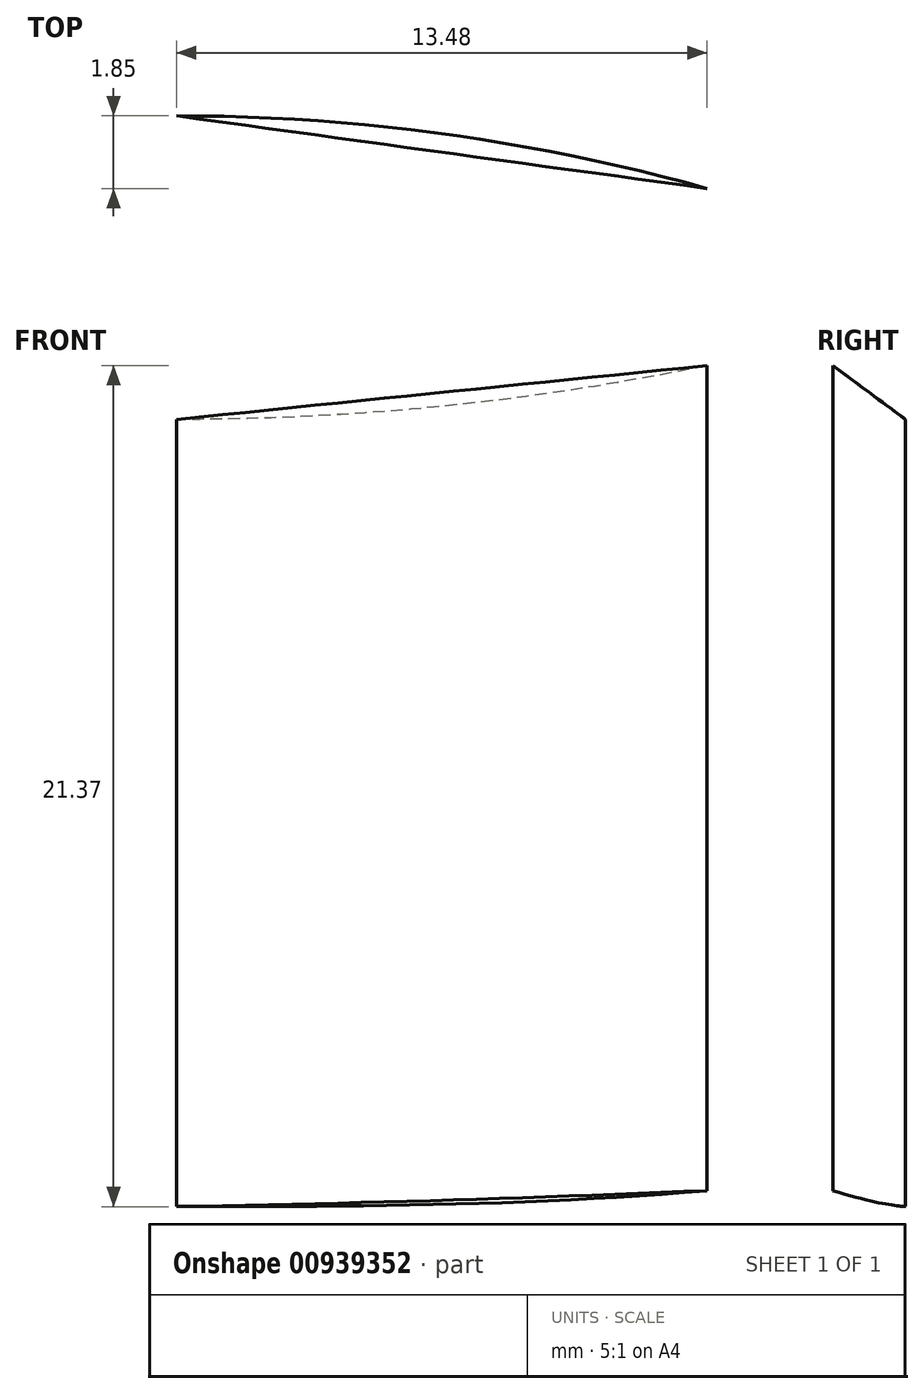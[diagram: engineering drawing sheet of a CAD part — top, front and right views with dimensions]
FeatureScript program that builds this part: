
annotation { "Feature Type Name" : "Feature", "Feature Type Description" : "" }
export const myFeature = defineFeature(function(context is Context, id is Id, definition is map)
    precondition{}
    {
        {
            var Q0;
            Q0=qCreatedBy(makeId("Top.planeOp"),FACE);
            var sketch = newSketch(context, id + "F0", { "sketchPlane" : qUnion([Q0])});
            skCircle(sketch, "E0", {"center": v(0, 0) * mm, "radius": 100 * mm, "construction": true});
            skLineSegment(sketch, "E1", {"start": v(0, 0) * mm, "end": v(4000, 0) * mm, "construction": true});
            skLineSegment(sketch, "E2", {"start": v(4000, 82.45) * mm, "end": v(4000, -88.42) * mm});
            skPoint(sketch, "E3.startSnap0", {"position": v(2000, 0) * mm});
            skEllipticalArc(sketch, "E4", {});
            skEllipticalArc(sketch, "E5", {});
            skLineSegment(sketch, "E6", {"start": v(500, 231.33) * mm, "end": v(500, -148.82) * mm, "construction": true});
            skLineSegment(sketch, "E7", {"start": v(2000, 216.5) * mm, "end": v(2000, -129.9) * mm, "construction": true});
            skLineSegment(sketch, "E8", {"start": v(3700, 95) * mm, "end": v(3700, -57) * mm, "construction": true});
            skFitSpline(sketch, "E9", {"points": [v(0, 100) * mm, v(166.45, 98.38) * mm, v(342.45, 195.8) * mm, v(973.63, 242.48) * mm], "startDerivative": vector(710.27, -109.76) * mm, "endDerivative": vector(1535.3, -24.16) * mm});
            skLineSegment(sketch, "E10", {"start": v(0, 100) * mm, "end": v(0, -150) * mm});
            const initialGuessF0  = {"E4": [0, 0, 1, 0, 4, 0.25, 0, 1.3393864335799355], "E5": [0, 0, 1, 0, 4, 0.15, 4.71238898038469, 0]};
            skSetInitialGuess(sketch, initialGuessF0);
            skSolve(sketch);
        }
        {
            var Q0;
            Q0=qCreatedBy(makeId("Right.planeOp"),FACE);
            cPlane(context, id + "F1", {"entities" : qUnion([Q0]), "cplaneType" : CPlaneType.OFFSET, "offset" : 500 * mm, "width" : 150 * mm, "height" : 150 * mm});
        }
        {
            var Q0;
            Q0=qCreatedBy(makeId("Right.planeOp"),FACE);
            cPlane(context, id + "F2", {"entities" : qUnion([Q0]), "cplaneType" : CPlaneType.OFFSET, "offset" : 2000 * mm, "width" : 150 * mm, "height" : 150 * mm});
        }
        {
            var Q0;
            Q0=qCreatedBy(makeId("Right.planeOp"),FACE);
            cPlane(context, id + "F3", {"entities" : qUnion([Q0]), "cplaneType" : CPlaneType.OFFSET, "offset" : 3800 * mm, "width" : 150 * mm, "height" : 150 * mm});
        }
        {
            var Q0;
            Q0=qCreatedBy(id+"F2.planeOp",FACE);
            var sketch = newSketch(context, id + "F4", { "sketchPlane" : qUnion([Q0])});
            skLineSegment(sketch, "E11.0", {"start": v(216.5, 0) * mm, "end": v(-129.9, 0) * mm, "construction": true});
            skFitSpline(sketch, "E12", {"points": [v(-51.98, 15.18) * mm, v(-51.7, 16.13) * mm, v(-51.37, 16.7) * mm, v(-50.56, 17.6) * mm, v(-49.8, 18.2) * mm, v(-48.48, 19) * mm, v(-46, 20.05) * mm, v(-43.86, 20.92) * mm, v(-42.48, 21.3) * mm, v(-40.4, 21.78) * mm, v(-35.9, 22.49) * mm, v(-32.06, 22.94) * mm, v(-26.66, 23.09) * mm, v(-18.94, 23.07) * mm, v(-15.53, 22.84) * mm, v(-7, 21.8) * mm, v(3.67, 20) * mm, v(18.13, 16.37) * mm, v(25.77, 13.8) * mm, v(33.1, 11.15) * mm, v(40.96, 7.91) * mm, v(48.22, 4.4) * mm, v(56.14, 0.25) * mm, v(63.47, -3.86) * mm, v(70.41, -7.7) * mm, v(87.44, -16.93) * mm, v(92.3, -19.6) * mm, v(98.84, -23.2) * mm, v(102.46, -25.25) * mm, v(104.38, -26.6) * mm], "startDerivative": vector(18.16, 67.2) * mm, "endDerivative": vector(76.76, -57.42) * mm});
            skFitSpline(sketch, "E13", {"points": [v(104.38, -26.6) * mm, v(101.9, -25.66) * mm, v(99.04, -24.5) * mm, v(93.95, -22.7) * mm, v(84, -20.33) * mm, v(74.92, -18.83) * mm, v(65.41, -17.67) * mm, v(56.36, -16.77) * mm, v(53.58, -16.66) * mm, v(49.7, -16.3) * mm, v(43.7, -15.98) * mm, v(35.25, -15.4) * mm, v(30.15, -15.15) * mm, v(23.5, -14.35) * mm, v(17.45, -13.49) * mm, v(10.23, -12.04) * mm, v(3.03, -10.4) * mm, v(-4.04, -8.4) * mm, v(-12.93, -5.58) * mm, v(-21.3, -2.57) * mm, v(-29.45, 0.5) * mm, v(-31.08, 1.2) * mm, v(-32.95, 2.14) * mm, v(-35.43, 3.32) * mm, v(-37.85, 4.54) * mm, v(-40.1, 5.61) * mm, v(-41.82, 6.54) * mm, v(-43.35, 7.39) * mm, v(-45, 8.3) * mm, v(-45.74, 8.81) * mm, v(-46.4, 9.33) * mm, v(-48.96, 11.2) * mm, v(-49.73, 11.89) * mm, v(-50.83, 12.86) * mm, v(-51.45, 13.6) * mm, v(-51.95, 14.4) * mm, v(-51.98, 15.18) * mm], "startDerivative": vector(-108.67, 41.14) * mm, "endDerivative": vector(7.25, 64.57) * mm});
            skLineSegment(sketch, "E14", {"start": v(3.86, 19.95) * mm, "end": v(-1.56, -9.14) * mm, "construction": true});
            skSolve(sketch);
        }
        {
            var Q0;
            Q0=qCreatedBy(id+"F3.planeOp",FACE);
            var sketch = newSketch(context, id + "F5", { "sketchPlane" : qUnion([Q0])});
            skFitSpline(sketch, "E15.1", {"points": [v(-52.9, 5.7) * mm, v(-52.86, 6.06) * mm, v(-52.8, 6.7) * mm, v(-52.58, 7.31) * mm, v(-51.92, 8.38) * mm, v(-51.26, 9.08) * mm, v(-50.1, 10.17) * mm, v(-47.85, 11.5) * mm, v(-45.94, 12.8) * mm, v(-44.55, 13.4) * mm, v(-42.58, 14.3) * mm, v(-38.21, 15.73) * mm, v(-34.56, 16.9) * mm, v(-29.42, 17.89) * mm, v(-21.6, 19.3) * mm, v(-18.38, 19.6) * mm, v(-9.12, 20.12) * mm, v(0.85, 20.3) * mm, v(15.94, 19.25) * mm, v(23.73, 17.85) * mm, v(31.65, 16.58) * mm, v(39.96, 14.77) * mm, v(47.68, 12.5) * mm, v(56.1, 9.87) * mm, v(64.46, 6.85) * mm, v(71.22, 4.54) * mm, v(90.24, -1.78) * mm, v(94.8, -3.34) * mm, v(102.25, -5.9) * mm, v(106.11, -7.17) * mm, v(107.68, -7.96) * mm, v(108.35, -8.3) * mm]});
            skFitSpline(sketch, "E15.2", {"points": [v(108.35, -8.3) * mm, v(107.49, -8.13) * mm, v(105.7, -7.8) * mm, v(102.56, -7.1) * mm, v(97.2, -6.07) * mm, v(87.02, -5.53) * mm, v(77.97, -5.69) * mm, v(68.82, -6.23) * mm, v(59.44, -6.84) * mm, v(56.68, -7.39) * mm, v(52.45, -7.59) * mm, v(46.79, -8.44) * mm, v(38.24, -9.17) * mm, v(33.4, -10.01) * mm, v(26.44, -10.26) * mm, v(20.48, -10.57) * mm, v(13.05, -10.3) * mm, v(5.66, -10.02) * mm, v(-1.6, -9.23) * mm, v(-11.05, -8) * mm, v(-19.05, -6.57) * mm, v(-28.04, -4.87) * mm, v(-29.8, -4.5) * mm, v(-31.94, -3.79) * mm, v(-34.56, -3.13) * mm, v(-37.1, -2.3) * mm, v(-39.52, -1.7) * mm, v(-41.38, -1.04) * mm, v(-43, -0.48) * mm, v(-44.79, 0.1) * mm, v(-45.67, 0.52) * mm, v(-46.35, 0.92) * mm, v(-49.33, 2.3) * mm, v(-50.02, 2.83) * mm, v(-51.42, 3.58) * mm, v(-52.05, 4.23) * mm, v(-52.84, 4.88) * mm, v(-52.88, 5.44) * mm, v(-52.9, 5.7) * mm]});
            skLineSegment(sketch, "E16", {"start": v(0.84, 20.11) * mm, "end": v(2.6, -9.67) * mm, "construction": true});
            skCircle(sketch, "E17", {"center": v(1.72, 5.22) * mm, "radius": 5.31 * mm, "construction": true});
            skSolve(sketch);
        }
        {
            var Q0;
            Q0=qCreatedBy(id+"F1.planeOp",FACE);
            var sketch = newSketch(context, id + "F6", { "sketchPlane" : qUnion([Q0])});
            skFitSpline(sketch, "E18.1", {"points": [v(-49.23, 22.19) * mm, v(-49.08, 22.5) * mm, v(-48.8, 23.09) * mm, v(-48.4, 23.6) * mm, v(-47.4, 24.37) * mm, v(-46.54, 24.8) * mm, v(-45.09, 25.42) * mm, v(-42.51, 25.91) * mm, v(-40.28, 26.47) * mm, v(-38.77, 26.56) * mm, v(-36.6, 26.74) * mm, v(-32, 26.58) * mm, v(-28.18, 26.44) * mm, v(-23, 25.6) * mm, v(-15.19, 24.25) * mm, v(-12.05, 23.45) * mm, v(-3.17, 20.75) * mm, v(6.26, 17.52) * mm, v(20.08, 11.37) * mm, v(26.92, 7.4) * mm, v(33.93, 3.49) * mm, v(41.12, -1.05) * mm, v(47.6, -5.82) * mm, v(54.6, -11.17) * mm, v(61.44, -16.87) * mm, v(67, -21.36) * mm, v(82.7, -33.8) * mm, v(86.46, -36.83) * mm, v(92.58, -41.8) * mm, v(95.78, -44.3) * mm, v(96.98, -45.57) * mm, v(97.5, -46.12) * mm]});
            skFitSpline(sketch, "E18.2", {"points": [v(97.5, -46.12) * mm, v(96.74, -45.67) * mm, v(95.18, -44.74) * mm, v(92.47, -43) * mm, v(87.77, -40.21) * mm, v(78.4, -36.23) * mm, v(69.84, -33.28) * mm, v(61.06, -30.66) * mm, v(52.03, -28.02) * mm, v(49.25, -27.6) * mm, v(45.21, -26.33) * mm, v(39.6, -25.2) * mm, v(31.31, -22.96) * mm, v(26.48, -22.1) * mm, v(19.85, -19.95) * mm, v(14.15, -18.2) * mm, v(7.26, -15.4) * mm, v(0.4, -12.62) * mm, v(-6.13, -9.4) * mm, v(-14.6, -5) * mm, v(-21.63, -0.92) * mm, v(-29.5, 3.74) * mm, v(-31.03, 4.7) * mm, v(-32.79, 6.1) * mm, v(-35.03, 7.61) * mm, v(-37.12, 9.26) * mm, v(-39.2, 10.66) * mm, v(-40.72, 11.9) * mm, v(-42.05, 13) * mm, v(-43.53, 14.15) * mm, v(-44.22, 14.85) * mm, v(-44.72, 15.45) * mm, v(-47.05, 17.76) * mm, v(-47.51, 18.5) * mm, v(-48.57, 19.69) * mm, v(-48.95, 20.51) * mm, v(-49.46, 21.4) * mm, v(-49.3, 21.93) * mm, v(-49.23, 22.19) * mm]});
            skPoint(sketch, "E19.0", {"position": v(-148.82, 0) * mm});
            skPoint(sketch, "E20.0", {"position": v(231.33, 0) * mm});
            skLineSegment(sketch, "E21", {"start": v(-4.69, -10.09) * mm, "end": v(7.77, 16.7) * mm, "construction": true});
            skLineSegment(sketch, "E22", {"start": v(-49.23, 22.19) * mm, "end": v(0, 0) * mm, "construction": true});
            skPoint(sketch, "E22.endSnap0", {"position": v(1.54, 3.3) * mm});
            skCircle(sketch, "E23", {"center": v(0, 0) * mm, "radius": 4 * mm, "construction": true});
            skLineSegment(sketch, "E24.0", {"start": v(-49.23, 22.19) * mm, "end": v(97.45, -46.21) * mm, "construction": true});
            skLineSegment(sketch, "E24.1", {"start": v(97.45, -46.21) * mm, "end": v(97.5, -46.12) * mm, "construction": true});
            skLineSegment(sketch, "E25.0", {"start": v(0, 0) * mm, "end": v(1.54, 3.3) * mm, "construction": true});
            skPoint(sketch, "E26", {"position": v(-2.5, 8.58) * mm});
            skSolve(sketch);
        }
        {
            var Q0;
            Q0=qCreatedBy(makeId("Right.planeOp"),FACE);
            var sketch = newSketch(context, id + "F7", { "sketchPlane" : qUnion([Q0])});
            skFitSpline(sketch, "E27.1", {"points": [v(-49.23, 22.19) * mm, v(-49.08, 22.5) * mm, v(-48.8, 23.09) * mm, v(-48.4, 23.6) * mm, v(-47.4, 24.37) * mm, v(-46.54, 24.8) * mm, v(-45.09, 25.42) * mm, v(-42.51, 25.91) * mm, v(-40.28, 26.47) * mm, v(-38.77, 26.56) * mm, v(-36.6, 26.74) * mm, v(-32, 26.58) * mm, v(-28.18, 26.44) * mm, v(-23, 25.6) * mm, v(-15.19, 24.25) * mm, v(-12.05, 23.45) * mm, v(-3.17, 20.75) * mm, v(6.26, 17.52) * mm, v(20.08, 11.37) * mm, v(26.92, 7.4) * mm, v(33.93, 3.49) * mm, v(41.12, -1.05) * mm, v(47.6, -5.82) * mm, v(54.6, -11.17) * mm, v(61.44, -16.87) * mm, v(67, -21.36) * mm, v(82.7, -33.8) * mm, v(86.46, -36.83) * mm, v(92.58, -41.8) * mm, v(95.78, -44.3) * mm, v(96.98, -45.57) * mm, v(97.5, -46.12) * mm]});
            skFitSpline(sketch, "E27.2", {"points": [v(97.5, -46.12) * mm, v(96.74, -45.67) * mm, v(95.18, -44.74) * mm, v(92.47, -43) * mm, v(87.77, -40.21) * mm, v(78.4, -36.23) * mm, v(69.84, -33.28) * mm, v(61.06, -30.66) * mm, v(52.03, -28.02) * mm, v(49.25, -27.6) * mm, v(45.21, -26.33) * mm, v(39.6, -25.2) * mm, v(31.31, -22.96) * mm, v(26.48, -22.1) * mm, v(19.85, -19.95) * mm, v(14.15, -18.2) * mm, v(7.26, -15.4) * mm, v(0.4, -12.62) * mm, v(-6.13, -9.4) * mm, v(-14.6, -5) * mm, v(-21.63, -0.92) * mm, v(-29.5, 3.74) * mm, v(-31.03, 4.7) * mm, v(-32.79, 6.1) * mm, v(-35.03, 7.61) * mm, v(-37.12, 9.26) * mm, v(-39.2, 10.66) * mm, v(-40.72, 11.9) * mm, v(-42.05, 13) * mm, v(-43.53, 14.15) * mm, v(-44.22, 14.85) * mm, v(-44.72, 15.45) * mm, v(-47.05, 17.76) * mm, v(-47.51, 18.5) * mm, v(-48.57, 19.69) * mm, v(-48.95, 20.51) * mm, v(-49.46, 21.4) * mm, v(-49.3, 21.93) * mm, v(-49.23, 22.19) * mm]});
            skSolve(sketch);
        }
        {
            var Q0;
            Q0=makeQuery(id+"F7.imprint","IMPRINT",FACE,{"disambiguationData":[TD([[makeQuery(id+"F7.imprint","IMPRINT",EDGE,{"derivedFrom":sQuery(id+"F7.wireOp",EDGE,"E27.1")}),-1.0]])]});
            var Q1;
            Q1=makeQuery(id+"F6.imprint","IMPRINT",FACE,{"disambiguationData":[TD([[makeQuery(id+"F6.imprint","IMPRINT",EDGE,{"derivedFrom":sQuery(id+"F6.wireOp",EDGE,"E18.1")}),-1.0]])]});
            var Q2;
            Q2=makeQuery(id+"F4.imprint","IMPRINT",FACE,{"disambiguationData":[TD([[makeQuery(id+"F4.imprint","IMPRINT",EDGE,{"derivedFrom":sQuery(id+"F4.wireOp",EDGE,"E12")}),-1.0]])]});
            var Q3;
            Q3=makeQuery(id+"F5.imprint","IMPRINT",FACE,{"disambiguationData":[TD([[makeQuery(id+"F5.imprint","IMPRINT",EDGE,{"derivedFrom":sQuery(id+"F5.wireOp",EDGE,"E15.1")}),-1.0]])]});
            loft(context, id + "F8", {"sheetProfilesArray" : [{ "sheetProfileEntities" : qUnion([Q0]) }, { "sheetProfileEntities" : qUnion([Q1]) }, { "sheetProfileEntities" : qUnion([Q2]) }, { "sheetProfileEntities" : qUnion([Q3]) }]});
        }
        {
            var Q0;
            Q0=qCreatedBy(makeId("Top.planeOp"),FACE);
            var sketch = newSketch(context, id + "F9", { "sketchPlane" : qUnion([Q0])});
            skArc(sketch, "E28", {"start": v(13.48, 48.34) * mm, "mid": v(6.8, 49.72) * mm, "end": v(0, 50.19) * mm});
            skFitSpline(sketch, "E29.0", {"points": [v(0, -49.23) * mm, v(79.17, -49.2) * mm, v(237.5, -49.16) * mm, v(475, -49.19) * mm, v(712.5, -49.4) * mm, v(1029.17, -49.9) * mm, v(1345.83, -50.6) * mm, v(1662.5, -51.32) * mm, v(1900, -51.81) * mm, v(2137.5, -52.21) * mm, v(2454.17, -52.6) * mm, v(2850, -52.86) * mm, v(3325, -52.94) * mm, v(3641.67, -52.9) * mm, v(3800, -52.9) * mm]});
            skFitSpline(sketch, "E30", {"points": [v(3800, 0) * mm, v(2820.14, 78.37) * mm, v(2106.22, 89.4) * mm, v(321.64, 65.97) * mm, v(274.87, 58.17) * mm, v(163.77, 38.68) * mm, v(0, 50.19) * mm], "startDerivative": vector(-4511.54, 397.19) * mm, "endDerivative": vector(-1676.25, 230.16) * mm});
            skLineSegment(sketch, "E31", {"start": v(0, -49.23) * mm, "end": v(0, 50.19) * mm});
            skFitSpline(sketch, "E32", {"points": [v(3013.33, -52.87) * mm, v(3164.93, -44.3) * mm, v(3178.72, -36.73) * mm, v(3189.74, -19.5) * mm, v(3191.12, 0) * mm, v(3175.96, 21.16) * mm, v(3130.48, 41.83) * mm, v(2995.47, 66.94) * mm], "startDerivative": vector(770.42, 19.14) * mm, "endDerivative": vector(-635.22, 97.5) * mm});
            skPoint(sketch, "E33.orphan", {"position": v(3800, -52.9) * mm});
            skLineSegment(sketch, "E34.bottom", {"start": v(4250.08, -757.9) * mm, "end": v(-833.94, -757.9) * mm});
            skLineSegment(sketch, "E34.top", {"start": v(4250.08, 716.67) * mm, "end": v(-833.94, 716.67) * mm});
            skLineSegment(sketch, "E34.left", {"start": v(4250.08, -757.9) * mm, "end": v(4250.08, 716.67) * mm});
            skLineSegment(sketch, "E34.right", {"start": v(-833.94, -757.9) * mm, "end": v(-833.94, 716.67) * mm});
            skSolve(sketch);
        }
        {
            var Q0;
            Q0 = qSketchRegion(id + "F9", true);
            extrude(context, id + "F10", {"entities" : qUnion([Q0]), "operationType" : NewBodyOperationType.REMOVE, "endBound" : BoundingType.SYMMETRIC, "oppositeDirection" : true, "depth" : 500 * mm, "offsetDistance" : 25 * mm});
        }
    });
